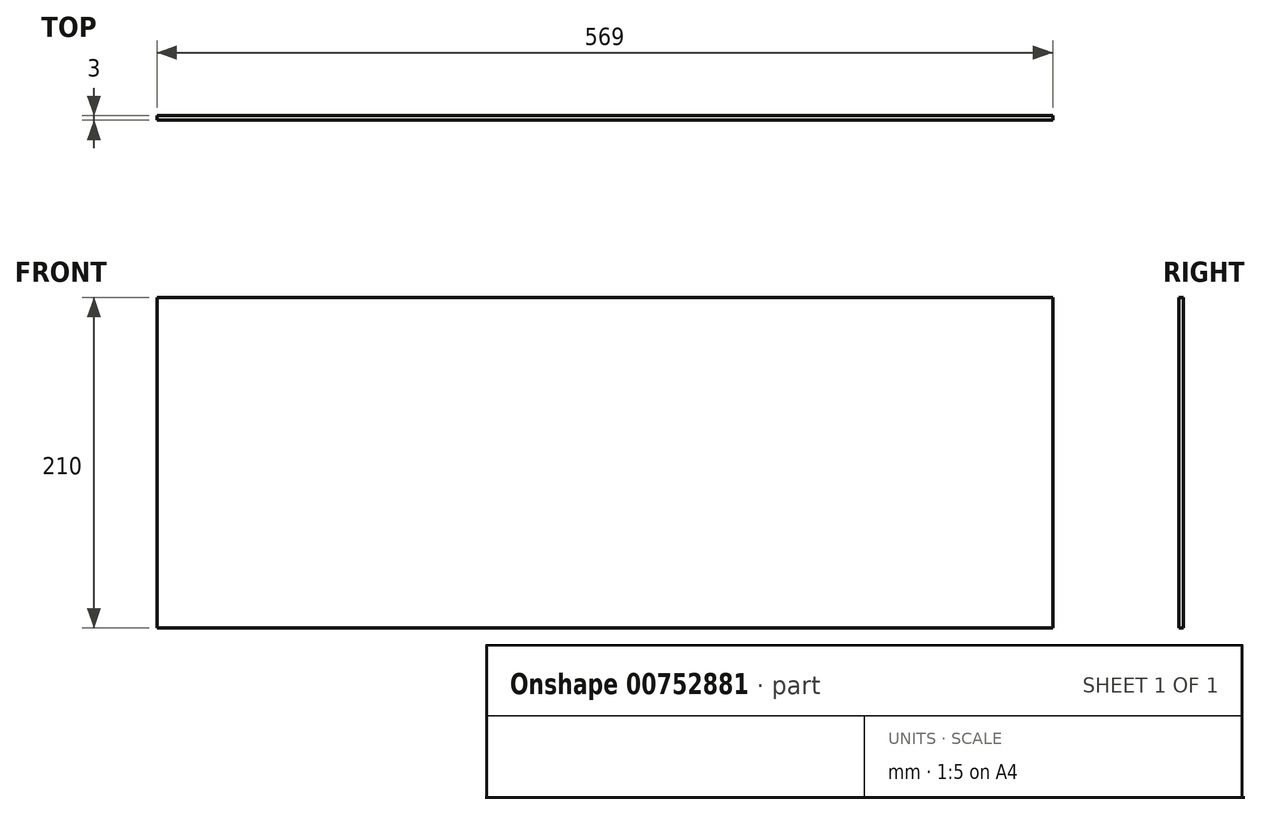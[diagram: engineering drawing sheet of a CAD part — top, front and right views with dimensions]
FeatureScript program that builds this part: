
annotation { "Feature Type Name" : "Feature", "Feature Type Description" : "" }
export const myFeature = defineFeature(function(context is Context, id is Id, definition is map)
    precondition{}
    {
        {
            var Q0;
            Q0=qCreatedBy(makeId("Front.planeOp"),FACE);
            var sketch = newSketch(context, id + "F0", { "sketchPlane" : qUnion([Q0])});
            skLineSegment(sketch, "E0.bottom", {"start": v(-284.5, 105) * mm, "end": v(284.5, 105) * mm});
            skLineSegment(sketch, "E0.top", {"start": v(-284.5, -105) * mm, "end": v(284.5, -105) * mm});
            skLineSegment(sketch, "E0.left", {"start": v(-284.5, 105) * mm, "end": v(-284.5, -105) * mm});
            skLineSegment(sketch, "E0.right", {"start": v(284.5, 105) * mm, "end": v(284.5, -105) * mm});
            skPoint(sketch, "E0.middle", {"position": v(0, 0) * mm});
            skSolve(sketch);
        }
        {
            var Q0;
            Q0=makeQuery(id+"F0.imprint","IMPRINT",FACE,{"disambiguationData":[TD([[makeQuery(id+"F0.imprint","IMPRINT",EDGE,{"derivedFrom":sQuery(id+"F0.wireOp",EDGE,"E0.bottom")}),-1.0]])]});
            extrude(context, id + "F1", {"entities" : qUnion([Q0]), "depth" : 3 * mm, "offsetDistance" : 25 * mm});
        }
    });
